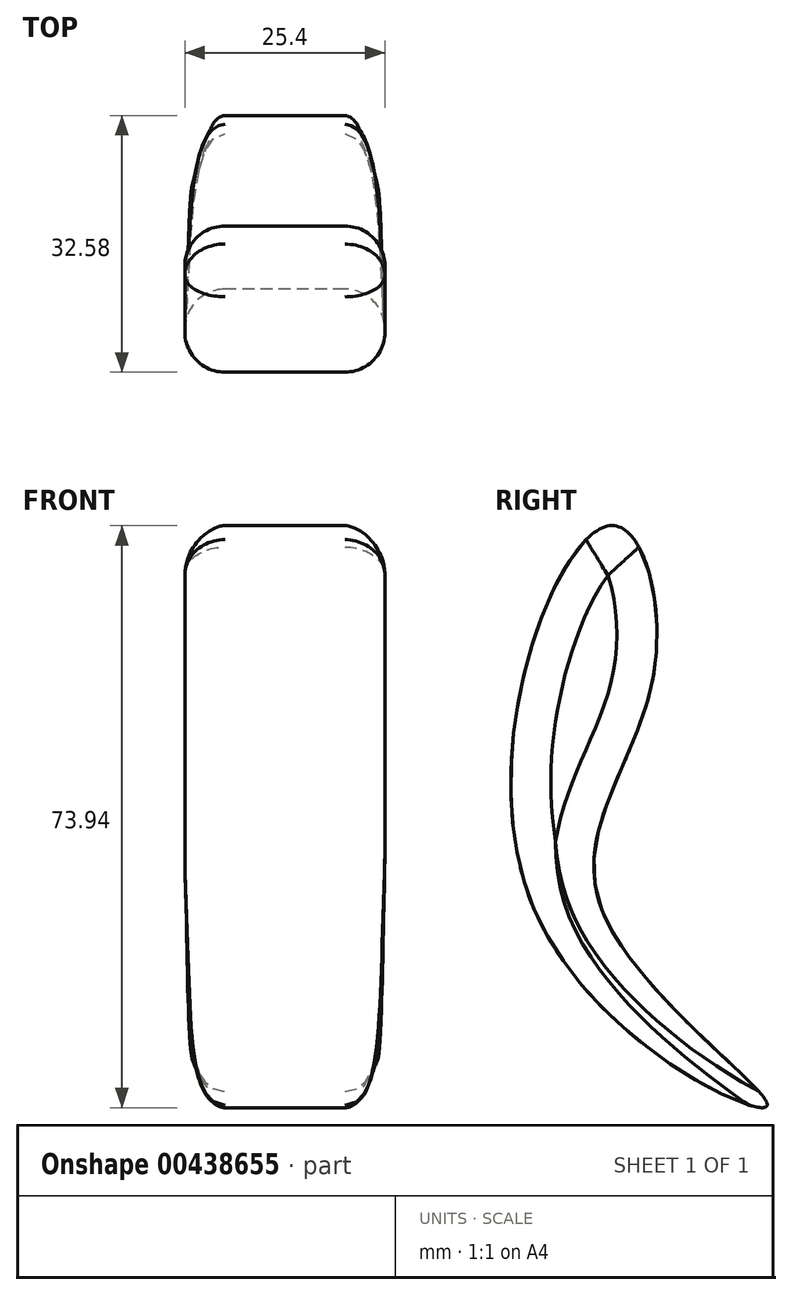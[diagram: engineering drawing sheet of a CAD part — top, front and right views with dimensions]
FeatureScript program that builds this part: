
annotation { "Feature Type Name" : "Feature", "Feature Type Description" : "" }
export const myFeature = defineFeature(function(context is Context, id is Id, definition is map)
    precondition{}
    {
        {
            var Q0;
            Q0=qCreatedBy(makeId("Right.planeOp"),FACE);
            var sketch = newSketch(context, id + "F0", { "sketchPlane" : qUnion([Q0])});
            skCircle(sketch, "E0", {"center": v(0, 0) * mm, "radius": 19 * mm});
            skFitSpline(sketch, "E1", {"points": [v(-7.4, -28.03) * mm, v(-37.14, -2.78) * mm, v(-27.4, 45.61) * mm, v(-21.85, 26.62) * mm, v(-28.4, -3.2) * mm, v(-7.4, -28.03) * mm]});
            skSolve(sketch);
        }
        {
            var Q0;
            Q0=makeQuery(id+"F0.imprint","IMPRINT",FACE,{"disambiguationData":[TD([[makeQuery(id+"F0.imprint","IMPRINT",EDGE,{"derivedFrom":sQuery(id+"F0.wireOp",EDGE,"E1")}),-1.0]])]});
            extrude(context, id + "F1", {"entities" : qUnion([Q0]), "depth" : 25.4 * mm});
        }
        {
            var Q0;
            Q0=makeQuery(id+"F1.opExtrude","CAP_EDGE",EDGE,{"disambiguationData":[OSD([sQuery(id+"F0.wireOp",EDGE,"E1")])],"isStart":false});
            var Q1;
            Q1=makeQuery(id+"F1.opExtrude","CAP_EDGE",EDGE,{"disambiguationData":[OSD([sQuery(id+"F0.wireOp",EDGE,"E1")])],"isStart":true});
            fillet(context, id + "F2", {"entities" : qUnion([Q0, Q1]), "radius" : 5.08 * mm, "tangentPropagation" : true, "allowEdgeOverflow" : false});
        }
    });
